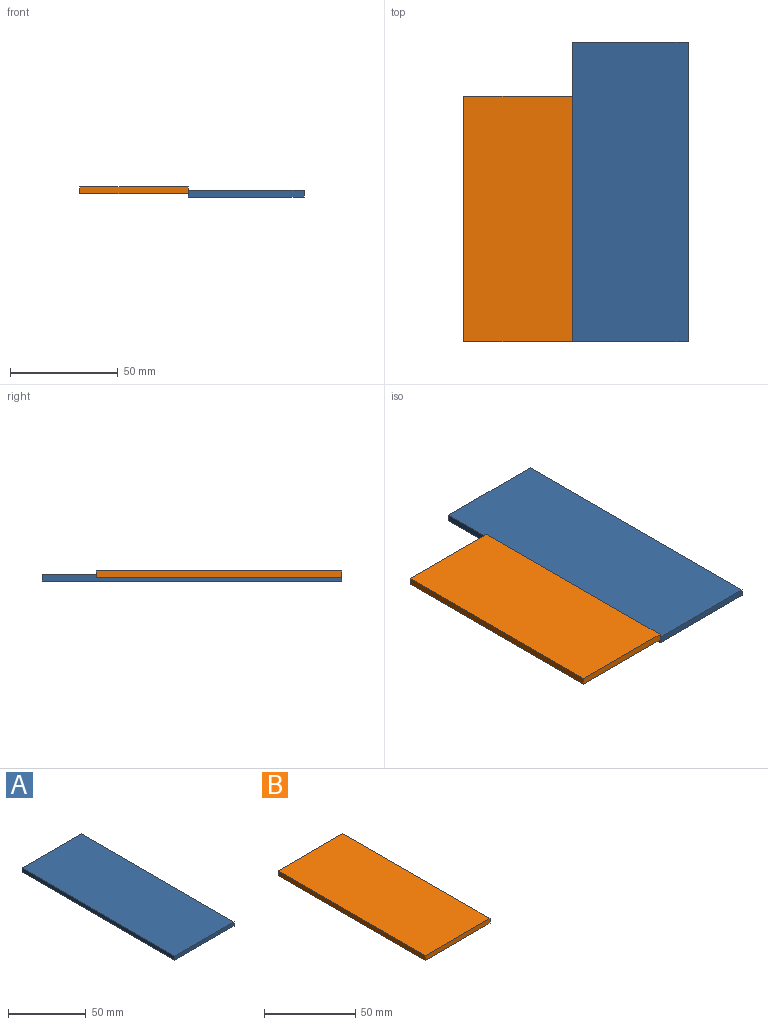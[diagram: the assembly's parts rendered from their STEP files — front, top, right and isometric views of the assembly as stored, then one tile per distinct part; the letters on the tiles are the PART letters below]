
ASSEMBLY  parts=2 mates=1
PART A: 6 faces, bbox 53.8x138.8x3.2 mm
  f0: plane 53.79x3.18mm, normal (0,1,0), area 170.8mm2, adj f1,f3,f4,f5
  f1: plane 138.8x3.18mm, normal (-1,0,0), area 440.7mm2, adj f0,f2,f4,f5
  f2: plane 53.79x3.18mm, normal (0,-1,0), area 170.8mm2, adj f1,f3,f4,f5
  f3: plane 138.8x3.18mm, normal (1,0,0), area 440.7mm2, adj f0,f2,f4,f5
  f4: plane 138.8x53.79mm, normal (0,0,1), area 7466.2mm2, adj f0,f1,f2,f3
  f5: plane 138.8x53.79mm, normal (0,0,-1), area 7466.2mm2, adj f0,f1,f2,f3
PART B: 6 faces, bbox 50.2x113.8x3.2 mm
  f0: plane 113.84x3.18mm, normal (1,0,0), area 361.4mm2, adj f1,f3,f4,f5
  f1: plane 50.23x3.18mm, normal (0,1,0), area 159.5mm2, adj f0,f2,f4,f5
  f2: plane 113.84x3.18mm, normal (-1,0,0), area 361.4mm2, adj f1,f3,f4,f5
  f3: plane 50.23x3.18mm, normal (0,-1,0), area 159.5mm2, adj f0,f2,f4,f5
  f4: plane 113.84x50.23mm, normal (0,0,1), area 5718.3mm2, adj f0,f1,f2,f3
  f5: plane 113.84x50.23mm, normal (0,0,-1), area 5718.3mm2, adj f0,f1,f2,f3
PLACE A at identity
PLACE B t=(0,0,1.59)mm
MATE revolute B.f3 <-> A.f2  axis (0,-1,0) through (0,0,3.18)mm
